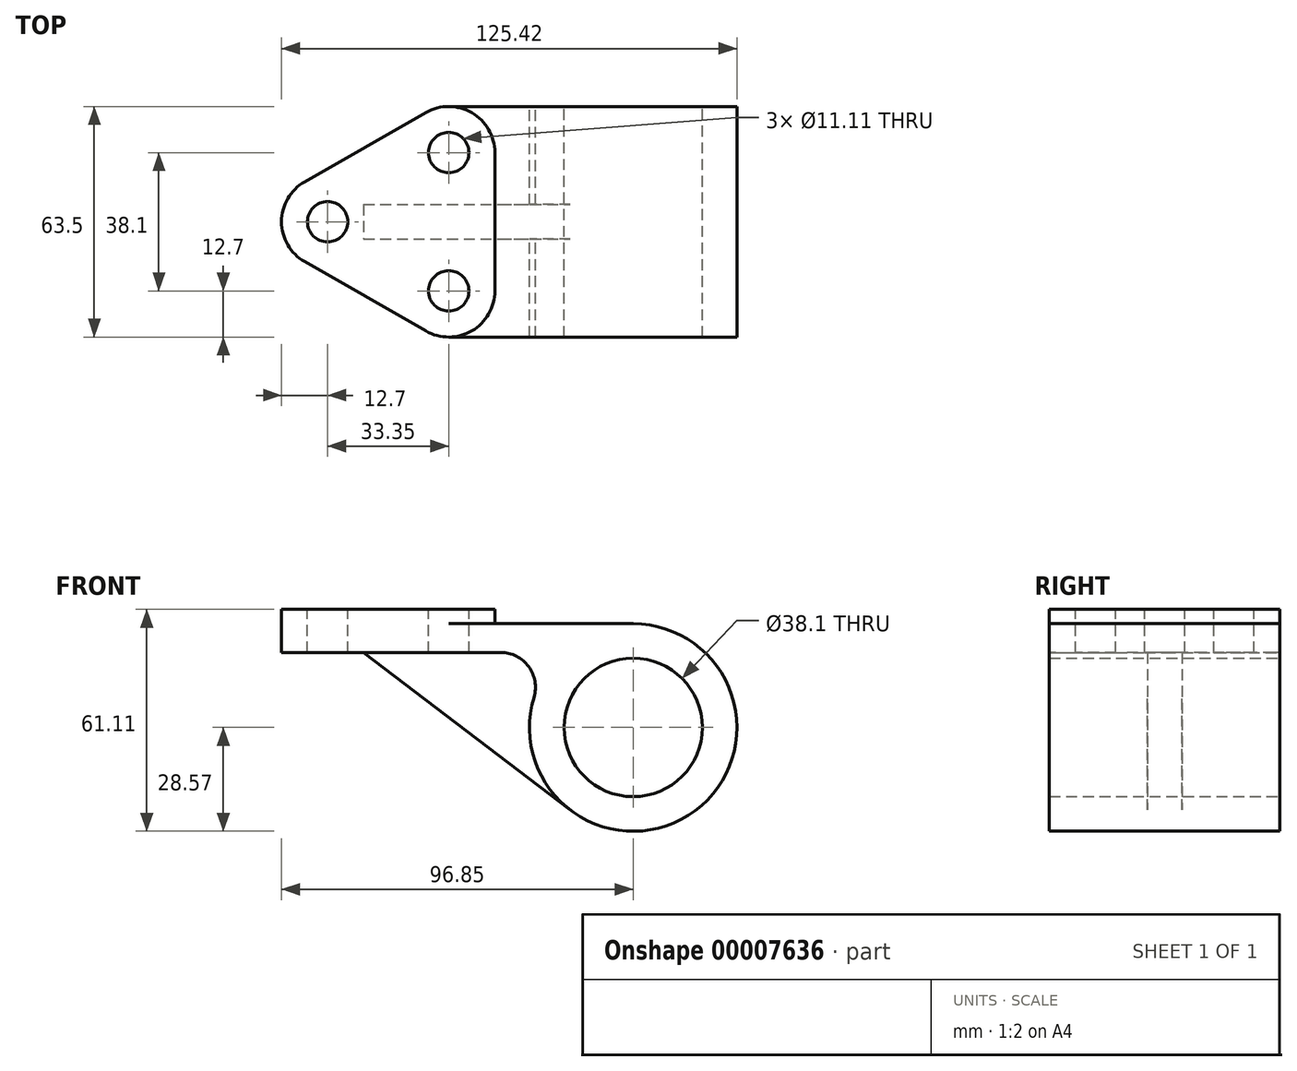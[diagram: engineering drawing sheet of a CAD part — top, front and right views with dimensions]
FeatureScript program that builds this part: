
annotation { "Feature Type Name" : "Feature", "Feature Type Description" : "" }
export const myFeature = defineFeature(function(context is Context, id is Id, definition is map)
    precondition{}
    {
        {
            var Q0;
            Q0=qCreatedBy(makeId("Front.planeOp"),FACE);
            var sketch = newSketch(context, id + "F0", { "sketchPlane" : qUnion([Q0])});
            skCircle(sketch, "E0", {"center": v(0, 0) * mm, "radius": 19.05 * mm});
            skArc(sketch, "E1", {"start": v(-27.33, 8.33) * mm, "mid": v(17, -22.96) * mm, "end": v(0, 28.58) * mm});
            skLineSegment(sketch, "E2", {"start": v(0, 28.58) * mm, "end": v(-50.8, 28.58) * mm});
            skLineSegment(sketch, "E3", {"start": v(-50.8, 28.57) * mm, "end": v(-50.8, 20.64) * mm});
            skLineSegment(sketch, "E4", {"start": v(-50.8, 20.64) * mm, "end": v(-36.44, 20.64) * mm});
            skPoint(sketch, "E5.visualSharp", {"position": v(-19.76, 20.64) * mm});
            skArc(sketch, "E5.filletArc", {"start": v(-27.33, 8.33) * mm, "mid": v(-28.79, 16.78) * mm, "end": v(-36.44, 20.64) * mm});
            skSolve(sketch);
        }
        {
            var Q0;
            Q0 = qSketchRegion(id + "F0", true);
            extrude(context, id + "F1", {"entities" : qUnion([Q0]), "depth" : 63.5 * mm, "symmetric" : true});
        }
        {
            var Q0;
            Q0=makeQuery(id+"F1.opExtrude","SWEPT_FACE",FACE,{"disambiguationData":[OSD([sQuery(id+"F0.wireOp",EDGE,"E2")])]});
            cPlane(context, id + "F2", {"entities" : qUnion([Q0]), "cplaneType" : CPlaneType.OFFSET, "offset" : 3.97 * mm, "width" : 152.4 * mm, "height" : 152.4 * mm});
        }
        {
            var Q0;
            Q0=qCreatedBy(id+"F2.planeOp",FACE);
            var sketch = newSketch(context, id + "F3", { "sketchPlane" : qUnion([Q0])});
            skCircle(sketch, "E6", {"center": v(-50.8, -19.05) * mm, "radius": 5.56 * mm});
            skCircle(sketch, "E7", {"center": v(-50.8, 19.05) * mm, "radius": 5.56 * mm});
            skCircle(sketch, "E8", {"center": v(-84.15, 0) * mm, "radius": 5.56 * mm});
            skLineSegment(sketch, "E9", {"start": v(0, 0) * mm, "end": v(-84.15, 0) * mm, "construction": true});
            skCircle(sketch, "E10", {"center": v(-50.8, 19.05) * mm, "radius": 12.7 * mm});
            skCircle(sketch, "E11", {"center": v(-50.8, -19.05) * mm, "radius": 12.7 * mm});
            skCircle(sketch, "E12", {"center": v(-84.15, 0) * mm, "radius": 12.7 * mm});
            skLineSegment(sketch, "E13", {"start": v(-90.45, 11.03) * mm, "end": v(-57.1, 30.08) * mm});
            skLineSegment(sketch, "E14", {"start": v(-90.45, -11.03) * mm, "end": v(-57.1, -30.08) * mm});
            skLineSegment(sketch, "E15", {"start": v(-38.1, 19.05) * mm, "end": v(-38.1, -19.05) * mm});
            skSolve(sketch);
        }
        {
            var Q0;
            Q0 = qSketchRegion(id + "F3", true);
            var Q1;
            Q1=makeQuery(id+"F1.opExtrude","SWEPT_FACE",FACE,{"disambiguationData":[OSD([sQuery(id+"F0.wireOp",EDGE,"E4")])]});
            extrude(context, id + "F4", {"entities" : qUnion([Q0]), "operationType" : NewBodyOperationType.ADD, "endBound" : BoundingType.UP_TO_SURFACE, "oppositeDirection" : true, "endBoundEntityFace" : qUnion([Q1]), "depth" : 25.4 * mm});
        }
        {
            var Q0;
            Q0=makeQuery(id+"F4.opExtrude","CAP_FACE",FACE,{"disambiguationData":[OSD([sQuery(id+"F3.wireOp",EDGE,"E6"),sQuery(id+"F3.wireOp",EDGE,"E7"),sQuery(id+"F3.wireOp",EDGE,"E8"),sQuery(id+"F3.wireOp",EDGE,"E10"),sQuery(id+"F3.wireOp",EDGE,"E11"),sQuery(id+"F3.wireOp",EDGE,"E12"),sQuery(id+"F3.wireOp",EDGE,"E13"),sQuery(id+"F3.wireOp",EDGE,"E14"),sQuery(id+"F3.wireOp",EDGE,"E15")])],"isStart":true});
            var sketch = newSketch(context, id + "F5", { "sketchPlane" : qUnion([Q0])});
            skCircle(sketch, "E16.0", {"center": v(-50.8, -19.05) * mm, "radius": 5.56 * mm});
            skCircle(sketch, "E16.1", {"center": v(-50.8, 19.05) * mm, "radius": 5.56 * mm});
            skSolve(sketch);
        }
        {
            var Q0;
            Q0 = qSketchRegion(id + "F5", true);
            extrude(context, id + "F6", {"entities" : qUnion([Q0]), "operationType" : NewBodyOperationType.REMOVE, "endBound" : BoundingType.THROUGH_ALL, "oppositeDirection" : true, "depth" : 25.4 * mm});
        }
        {
            var Q0;
            Q0=qCreatedBy(makeId("Front.planeOp"),FACE);
            var sketch = newSketch(context, id + "F7", { "sketchPlane" : qUnion([Q0])});
            skLineSegment(sketch, "E17", {"start": v(-20.18, -20.55) * mm, "end": v(-74.24, 20.64) * mm});
            skSolve(sketch);
        }
        {
            var Q0;
            Q0=sQuery(id+"F7.wireOp",EDGE,"E17");
            cPlane(context, id + "F8", {"entities" : qUnion([Q0]), "cplaneType" : CPlaneType.LINE_ANGLE, "offset" : 152.4 * mm, "angle" : 90 * degree, "width" : 152.4 * mm, "height" : 152.4 * mm});
        }
        {
            var Q0;
            Q0=qCreatedBy(id+"F8.planeOp",FACE);
            var sketch = newSketch(context, id + "F9", { "sketchPlane" : qUnion([Q0])});
            skLineSegment(sketch, "E18.bottom", {"start": v(-71.56, 4.76) * mm, "end": v(0, 4.76) * mm});
            skLineSegment(sketch, "E18.top", {"start": v(-71.56, -4.76) * mm, "end": v(0, -4.76) * mm});
            skLineSegment(sketch, "E18.left", {"start": v(-71.56, 4.76) * mm, "end": v(-71.56, -4.76) * mm});
            skLineSegment(sketch, "E18.right", {"start": v(0, 4.76) * mm, "end": v(0, -4.76) * mm});
            skSolve(sketch);
        }
        {
            var Q0;
            Q0 = qSketchRegion(id + "F9", true);
            var Q1;
            {var subQ0=sQuery(id+"F0.wireOp",EDGE,"E4");Q1=makeQuery(id+"F4.boolean.opBoolean","MERGE",FACE,{"derivedFrom":[makeQuery(id+"F1.opExtrude","SWEPT_FACE",FACE,{"disambiguationData":[OSD([subQ0])]}),makeQuery(id+"F4.opExtrude","CAP_FACE",FACE,{"disambiguationData":[OSD([subQ0])],"isStart":false})]});}
            extrude(context, id + "F10", {"entities" : qUnion([Q0]), "operationType" : NewBodyOperationType.ADD, "endBound" : BoundingType.UP_TO_NEXT, "endBoundEntity" : qUnion([Q1]), "depth" : 25.4 * mm});
        }
    });
